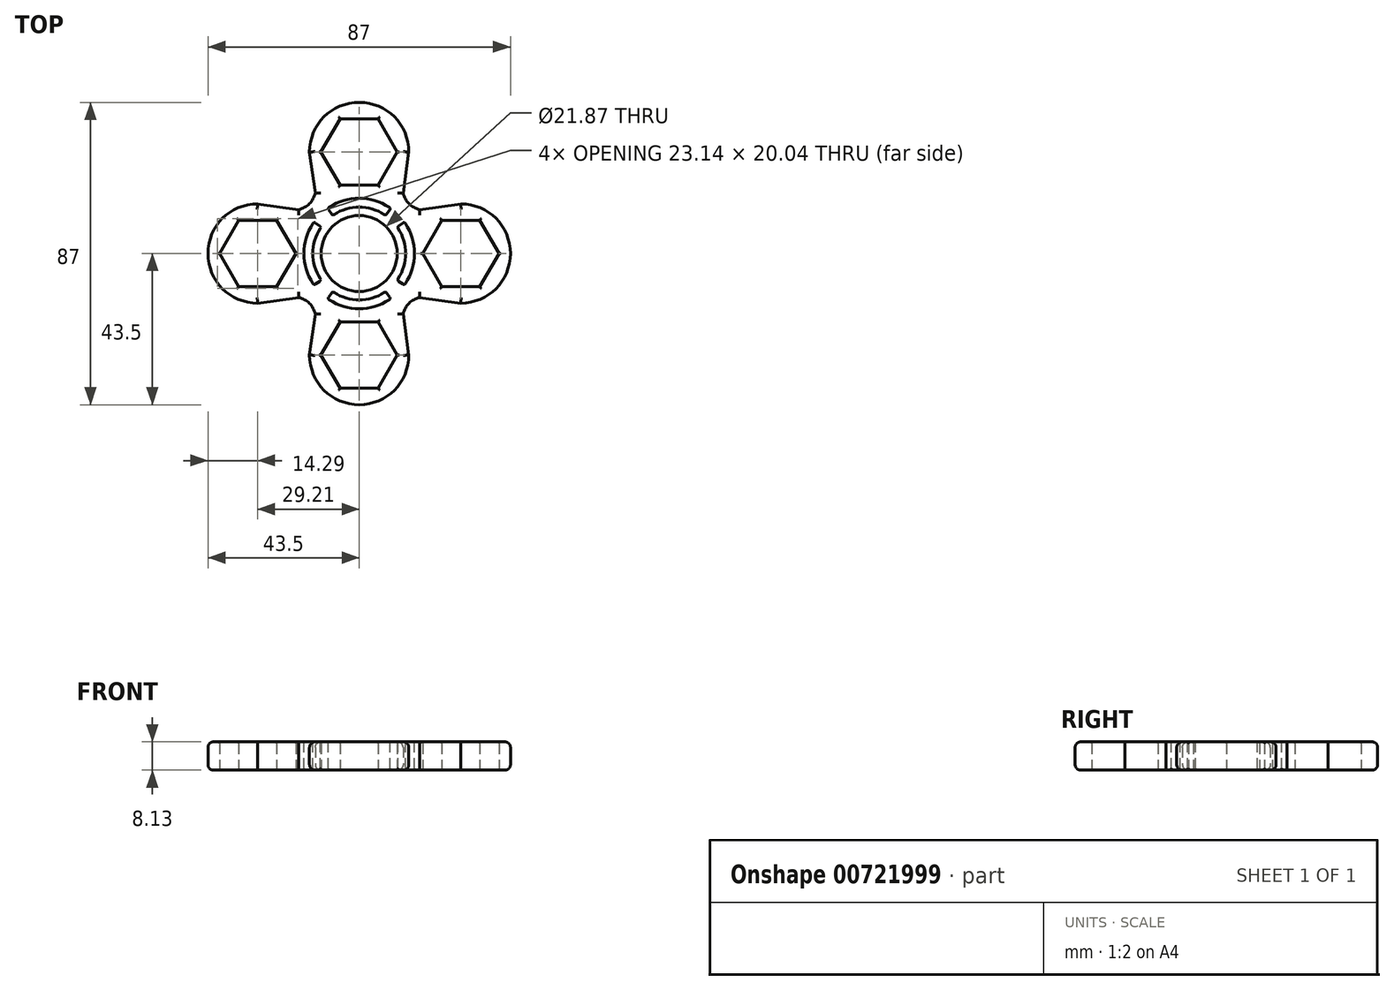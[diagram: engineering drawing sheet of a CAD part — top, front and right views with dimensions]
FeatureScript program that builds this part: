
annotation { "Feature Type Name" : "Feature", "Feature Type Description" : "" }
export const myFeature = defineFeature(function(context is Context, id is Id, definition is map)
    precondition{}
    {
        {
            var Q0;
            Q0=qCreatedBy(makeId("Top.planeOp"),FACE);
            var sketch = newSketch(context, id + "F0", { "sketchPlane" : qUnion([Q0])});
            skCircle(sketch, "E0", {"center": v(0, 0) * mm, "radius": 10.93 * mm});
            skLineSegment(sketch, "E1", {"start": v(0, 32.8) * mm, "end": v(0, -37.97) * mm, "construction": true});
            skLineSegment(sketch, "E2", {"start": v(-47.87, 0) * mm, "end": v(62.97, 0) * mm, "construction": true});
            skCircle(sketch, "E3", {"center": v(29.21, 0) * mm, "radius": 7.94 * mm});
            skCircle(sketch, "E4", {"center": v(0, 29.21) * mm, "radius": 7.94 * mm});
            skCircle(sketch, "E5", {"center": v(-29.21, 0) * mm, "radius": 7.94 * mm});
            skCircle(sketch, "E6", {"center": v(0, -29.21) * mm, "radius": 7.94 * mm});
            skArc(sketch, "E7", {"start": v(14.29, 29.21) * mm, "mid": v(0, 43.5) * mm, "end": v(-14.29, 29.21) * mm});
            skArc(sketch, "E8", {"start": v(29.21, -14.29) * mm, "mid": v(43.5, 0) * mm, "end": v(29.21, 14.29) * mm});
            skArc(sketch, "E9", {"start": v(-14.29, -29.21) * mm, "mid": v(0, -43.5) * mm, "end": v(14.29, -29.21) * mm});
            skArc(sketch, "E10", {"start": v(-29.21, 14.29) * mm, "mid": v(-43.5, 0) * mm, "end": v(-29.21, -14.29) * mm});
            skPoint(sketch, "E11.visualSharp", {"position": v(-11.05, 11.05) * mm});
            skArc(sketch, "E11.filletArc", {"start": v(-17.4, 12.64) * mm, "mid": v(-14.33, 14.33) * mm, "end": v(-12.64, 17.4) * mm});
            skPoint(sketch, "E12.visualSharp", {"position": v(11.05, 11.05) * mm});
            skArc(sketch, "E12.filletArc", {"start": v(12.64, 17.4) * mm, "mid": v(14.33, 14.33) * mm, "end": v(17.4, 12.64) * mm});
            skArc(sketch, "E13.MirrorCS", {"start": v(-17.4, -12.64) * mm, "mid": v(-14.33, -14.33) * mm, "end": v(-12.64, -17.4) * mm});
            skArc(sketch, "E14.MirrorCS", {"start": v(12.64, -17.4) * mm, "mid": v(14.33, -14.33) * mm, "end": v(17.4, -12.64) * mm});
            skLineSegment(sketch, "E15", {"start": v(-14.29, -29.21) * mm, "end": v(-12.64, -17.4) * mm});
            skLineSegment(sketch, "E16", {"start": v(14.29, -29.2) * mm, "end": v(12.64, -17.4) * mm});
            skLineSegment(sketch, "E17", {"start": v(17.4, -12.64) * mm, "end": v(29.21, -14.29) * mm});
            skLineSegment(sketch, "E18", {"start": v(17.4, 12.64) * mm, "end": v(29.21, 14.29) * mm});
            skLineSegment(sketch, "E19", {"start": v(12.64, 17.4) * mm, "end": v(14.29, 29.21) * mm});
            skLineSegment(sketch, "E20", {"start": v(-14.29, 29.21) * mm, "end": v(-12.64, 17.4) * mm});
            skLineSegment(sketch, "E21", {"start": v(-17.4, 12.64) * mm, "end": v(-29.2, 14.29) * mm});
            skLineSegment(sketch, "E22", {"start": v(-29.2, -14.29) * mm, "end": v(-17.4, -12.64) * mm});
            skCircle(sketch, "E23.cCircle", {"center": v(0, 29.21) * mm, "radius": 9.51 * mm, "construction": true});
            skLineSegment(sketch, "E23.0", {"start": v(10.99, 29.21) * mm, "end": v(5.5, 19.7) * mm});
            skLineSegment(sketch, "E23.1", {"start": v(5.5, 19.7) * mm, "end": v(-5.5, 19.7) * mm});
            skLineSegment(sketch, "E23.2", {"start": v(-5.5, 19.7) * mm, "end": v(-10.99, 29.21) * mm});
            skLineSegment(sketch, "E23.3", {"start": v(-10.99, 29.21) * mm, "end": v(-5.5, 38.72) * mm});
            skLineSegment(sketch, "E23.4", {"start": v(-5.5, 38.72) * mm, "end": v(5.5, 38.72) * mm});
            skLineSegment(sketch, "E23.5", {"start": v(5.5, 38.72) * mm, "end": v(10.99, 29.21) * mm});
            skPoint(sketch, "E23.0.midPoint", {"position": v(8.24, 24.45) * mm});
            skCircle(sketch, "E24.cCircle", {"center": v(29.21, 0) * mm, "radius": 9.51 * mm, "construction": true});
            skLineSegment(sketch, "E24.0", {"start": v(40.2, 0) * mm, "end": v(34.7, -9.51) * mm});
            skLineSegment(sketch, "E24.1", {"start": v(34.7, -9.51) * mm, "end": v(23.72, -9.51) * mm});
            skLineSegment(sketch, "E24.2", {"start": v(23.72, -9.51) * mm, "end": v(18.22, 0) * mm});
            skLineSegment(sketch, "E24.3", {"start": v(18.22, 0) * mm, "end": v(23.72, 9.51) * mm});
            skLineSegment(sketch, "E24.4", {"start": v(23.72, 9.51) * mm, "end": v(34.7, 9.51) * mm});
            skLineSegment(sketch, "E24.5", {"start": v(34.7, 9.51) * mm, "end": v(40.2, 0) * mm});
            skPoint(sketch, "E24.0.midPoint", {"position": v(37.45, -4.76) * mm});
            skCircle(sketch, "E25.cCircle", {"center": v(0, -29.21) * mm, "radius": 9.51 * mm, "construction": true});
            skLineSegment(sketch, "E25.0", {"start": v(10.99, -29.2) * mm, "end": v(5.5, -38.72) * mm});
            skLineSegment(sketch, "E25.1", {"start": v(5.5, -38.72) * mm, "end": v(-5.5, -38.72) * mm});
            skLineSegment(sketch, "E25.2", {"start": v(-5.5, -38.72) * mm, "end": v(-10.99, -29.2) * mm});
            skLineSegment(sketch, "E25.3", {"start": v(-10.99, -29.21) * mm, "end": v(-5.5, -19.7) * mm});
            skLineSegment(sketch, "E25.4", {"start": v(-5.5, -19.7) * mm, "end": v(5.5, -19.7) * mm});
            skLineSegment(sketch, "E25.5", {"start": v(5.5, -19.7) * mm, "end": v(10.99, -29.21) * mm});
            skPoint(sketch, "E25.0.midPoint", {"position": v(8.24, -33.97) * mm});
            skPoint(sketch, "E26.0.midPoint", {"position": v(-0.58, -16.53) * mm});
            skCircle(sketch, "E27.cCircle", {"center": v(-29.21, 0) * mm, "radius": 9.51 * mm, "construction": true});
            skLineSegment(sketch, "E27.0", {"start": v(-18.22, 0) * mm, "end": v(-23.72, -9.51) * mm});
            skLineSegment(sketch, "E27.1", {"start": v(-23.72, -9.51) * mm, "end": v(-34.7, -9.51) * mm});
            skLineSegment(sketch, "E27.2", {"start": v(-34.7, -9.51) * mm, "end": v(-40.2, 0) * mm});
            skLineSegment(sketch, "E27.3", {"start": v(-40.2, 0) * mm, "end": v(-34.7, 9.51) * mm});
            skLineSegment(sketch, "E27.4", {"start": v(-34.7, 9.51) * mm, "end": v(-23.72, 9.51) * mm});
            skLineSegment(sketch, "E27.5", {"start": v(-23.72, 9.51) * mm, "end": v(-18.22, 0) * mm});
            skPoint(sketch, "E27.0.midPoint", {"position": v(-20.97, -4.76) * mm});
            skSolve(sketch);
        }
        {
            var Q0;
            Q0=qSketchRegion(id+"F0",true);
            extrude(context, id + "F1", {"entities" : qUnion([Q0]), "depth" : 8.13 * mm, "offsetDistance" : 25.4 * mm});
        }
        {
            var Q0;
            Q0=makeQuery(id+"F1.opExtrude","CAP_EDGE",EDGE,{"disambiguationData":[OSD([sQuery(id+"F0.wireOp",EDGE,"E10")])],"isStart":true});
            var Q1;
            Q1=makeQuery(id+"F1.opExtrude","CAP_EDGE",EDGE,{"disambiguationData":[OSD([sQuery(id+"F0.wireOp",EDGE,"E22")])],"isStart":true});
            var Q2;
            Q2=makeQuery(id+"F1.opExtrude","CAP_EDGE",EDGE,{"disambiguationData":[OSD([sQuery(id+"F0.wireOp",EDGE,"E13.MirrorCS")])],"isStart":true});
            var Q3;
            Q3=makeQuery(id+"F1.opExtrude","CAP_EDGE",EDGE,{"disambiguationData":[OSD([sQuery(id+"F0.wireOp",EDGE,"E15")])],"isStart":true});
            var Q4;
            Q4=makeQuery(id+"F1.opExtrude","CAP_EDGE",EDGE,{"disambiguationData":[OSD([sQuery(id+"F0.wireOp",EDGE,"E9")])],"isStart":true});
            var Q5;
            Q5=makeQuery(id+"F1.opExtrude","CAP_EDGE",EDGE,{"disambiguationData":[OSD([sQuery(id+"F0.wireOp",EDGE,"E16")])],"isStart":true});
            var Q6;
            Q6=makeQuery(id+"F1.opExtrude","CAP_EDGE",EDGE,{"disambiguationData":[OSD([sQuery(id+"F0.wireOp",EDGE,"E14.MirrorCS")])],"isStart":true});
            var Q7;
            Q7=makeQuery(id+"F1.opExtrude","CAP_EDGE",EDGE,{"disambiguationData":[OSD([sQuery(id+"F0.wireOp",EDGE,"E17")])],"isStart":true});
            var Q8;
            Q8=makeQuery(id+"F1.opExtrude","CAP_EDGE",EDGE,{"disambiguationData":[OSD([sQuery(id+"F0.wireOp",EDGE,"E8")])],"isStart":true});
            var Q9;
            Q9=makeQuery(id+"F1.opExtrude","CAP_EDGE",EDGE,{"disambiguationData":[OSD([sQuery(id+"F0.wireOp",EDGE,"E18")])],"isStart":true});
            var Q10;
            Q10=makeQuery(id+"F1.opExtrude","CAP_EDGE",EDGE,{"disambiguationData":[OSD([sQuery(id+"F0.wireOp",EDGE,"E12.filletArc")])],"isStart":true});
            var Q11;
            Q11=makeQuery(id+"F1.opExtrude","CAP_EDGE",EDGE,{"disambiguationData":[OSD([sQuery(id+"F0.wireOp",EDGE,"E19")])],"isStart":true});
            var Q12;
            Q12=makeQuery(id+"F1.opExtrude","CAP_EDGE",EDGE,{"disambiguationData":[OSD([sQuery(id+"F0.wireOp",EDGE,"E7")])],"isStart":true});
            var Q13;
            Q13=makeQuery(id+"F1.opExtrude","CAP_EDGE",EDGE,{"disambiguationData":[OSD([sQuery(id+"F0.wireOp",EDGE,"E20")])],"isStart":true});
            var Q14;
            Q14=makeQuery(id+"F1.opExtrude","CAP_EDGE",EDGE,{"disambiguationData":[OSD([sQuery(id+"F0.wireOp",EDGE,"E11.filletArc")])],"isStart":true});
            var Q15;
            Q15=makeQuery(id+"F1.opExtrude","CAP_EDGE",EDGE,{"disambiguationData":[OSD([sQuery(id+"F0.wireOp",EDGE,"E21")])],"isStart":true});
            var Q16;
            Q16=makeQuery(id+"F1.opExtrude","CAP_EDGE",EDGE,{"disambiguationData":[OSD([sQuery(id+"F0.wireOp",EDGE,"E10")])],"isStart":false});
            var Q17;
            Q17=makeQuery(id+"F1.opExtrude","CAP_EDGE",EDGE,{"disambiguationData":[OSD([sQuery(id+"F0.wireOp",EDGE,"E22")])],"isStart":false});
            var Q18;
            Q18=makeQuery(id+"F1.opExtrude","CAP_EDGE",EDGE,{"disambiguationData":[OSD([sQuery(id+"F0.wireOp",EDGE,"E13.MirrorCS")])],"isStart":false});
            var Q19;
            Q19=makeQuery(id+"F1.opExtrude","CAP_EDGE",EDGE,{"disambiguationData":[OSD([sQuery(id+"F0.wireOp",EDGE,"E21")])],"isStart":false});
            var Q20;
            Q20=makeQuery(id+"F1.opExtrude","CAP_EDGE",EDGE,{"disambiguationData":[OSD([sQuery(id+"F0.wireOp",EDGE,"E11.filletArc")])],"isStart":false});
            var Q21;
            Q21=makeQuery(id+"F1.opExtrude","CAP_EDGE",EDGE,{"disambiguationData":[OSD([sQuery(id+"F0.wireOp",EDGE,"E20")])],"isStart":false});
            var Q22;
            Q22=makeQuery(id+"F1.opExtrude","CAP_EDGE",EDGE,{"disambiguationData":[OSD([sQuery(id+"F0.wireOp",EDGE,"E7")])],"isStart":false});
            var Q23;
            Q23=makeQuery(id+"F1.opExtrude","CAP_EDGE",EDGE,{"disambiguationData":[OSD([sQuery(id+"F0.wireOp",EDGE,"E19")])],"isStart":false});
            var Q24;
            Q24=makeQuery(id+"F1.opExtrude","CAP_EDGE",EDGE,{"disambiguationData":[OSD([sQuery(id+"F0.wireOp",EDGE,"E8")])],"isStart":false});
            var Q25;
            Q25=makeQuery(id+"F1.opExtrude","CAP_EDGE",EDGE,{"disambiguationData":[OSD([sQuery(id+"F0.wireOp",EDGE,"E17")])],"isStart":false});
            var Q26;
            Q26=makeQuery(id+"F1.opExtrude","CAP_EDGE",EDGE,{"disambiguationData":[OSD([sQuery(id+"F0.wireOp",EDGE,"E14.MirrorCS")])],"isStart":false});
            var Q27;
            Q27=makeQuery(id+"F1.opExtrude","CAP_EDGE",EDGE,{"disambiguationData":[OSD([sQuery(id+"F0.wireOp",EDGE,"E16")])],"isStart":false});
            var Q28;
            Q28=makeQuery(id+"F1.opExtrude","CAP_EDGE",EDGE,{"disambiguationData":[OSD([sQuery(id+"F0.wireOp",EDGE,"E9")])],"isStart":false});
            var Q29;
            Q29=makeQuery(id+"F1.opExtrude","CAP_EDGE",EDGE,{"disambiguationData":[OSD([sQuery(id+"F0.wireOp",EDGE,"E15")])],"isStart":false});
            var Q30;
            Q30=makeQuery(id+"F1.opExtrude","CAP_EDGE",EDGE,{"disambiguationData":[OSD([sQuery(id+"F0.wireOp",EDGE,"E12.filletArc")])],"isStart":false});
            var Q31;
            Q31=makeQuery(id+"F1.opExtrude","CAP_EDGE",EDGE,{"disambiguationData":[OSD([sQuery(id+"F0.wireOp",EDGE,"E18")])],"isStart":false});
            fillet(context, id + "F2", {"entities" : qUnion([Q0, Q1, Q2, Q3, Q4, Q5, Q6, Q7, Q8, Q9, Q10, Q11, Q12, Q13, Q14, Q15, Q16, Q17, Q18, Q19, Q20, Q21, Q22, Q23, Q24, Q25, Q26, Q27, Q28, Q29, Q30, Q31]), "radius" : 1.57 * mm, "allowEdgeOverflow" : false});
        }
        {
            var Q0;
            Q0=makeQuery(id+"F1.opExtrude","CAP_EDGE",EDGE,{"disambiguationData":[OSD([sQuery(id+"F0.wireOp",EDGE,"E5")])],"isStart":false});
            var Q1;
            Q1=makeQuery(id+"F1.opExtrude","CAP_EDGE",EDGE,{"disambiguationData":[OSD([sQuery(id+"F0.wireOp",EDGE,"E4")])],"isStart":false});
            var Q2;
            Q2=makeQuery(id+"F1.opExtrude","CAP_EDGE",EDGE,{"disambiguationData":[OSD([sQuery(id+"F0.wireOp",EDGE,"E0")])],"isStart":false});
            var Q3;
            Q3=makeQuery(id+"F1.opExtrude","CAP_EDGE",EDGE,{"disambiguationData":[OSD([sQuery(id+"F0.wireOp",EDGE,"E3")])],"isStart":false});
            var Q4;
            Q4=makeQuery(id+"F1.opExtrude","CAP_EDGE",EDGE,{"disambiguationData":[OSD([sQuery(id+"F0.wireOp",EDGE,"E6")])],"isStart":false});
            var Q5;
            Q5=makeQuery(id+"F1.opExtrude","CAP_EDGE",EDGE,{"disambiguationData":[OSD([sQuery(id+"F0.wireOp",EDGE,"E6")])],"isStart":true});
            var Q6;
            Q6=makeQuery(id+"F1.opExtrude","CAP_EDGE",EDGE,{"disambiguationData":[OSD([sQuery(id+"F0.wireOp",EDGE,"E5")])],"isStart":true});
            var Q7;
            Q7=makeQuery(id+"F1.opExtrude","CAP_EDGE",EDGE,{"disambiguationData":[OSD([sQuery(id+"F0.wireOp",EDGE,"E0")])],"isStart":true});
            var Q8;
            Q8=makeQuery(id+"F1.opExtrude","CAP_EDGE",EDGE,{"disambiguationData":[OSD([sQuery(id+"F0.wireOp",EDGE,"E3")])],"isStart":true});
            var Q9;
            Q9=makeQuery(id+"F1.opExtrude","CAP_EDGE",EDGE,{"disambiguationData":[OSD([sQuery(id+"F0.wireOp",EDGE,"E4")])],"isStart":true});
            fillet(context, id + "F3", {"entities" : qUnion([Q0, Q1, Q2, Q3, Q4, Q5, Q6, Q7, Q8, Q9]), "radius" : 0.5 * mm, "tangentPropagation" : true, "allowEdgeOverflow" : false});
        }
        {
            var Q0;
            Q0=makeQuery(id+"F1.opExtrude","CAP_EDGE",EDGE,{"disambiguationData":[OSD([sQuery(id+"F0.wireOp",EDGE,"E25.4")])],"isStart":false});
            var Q1;
            Q1=makeQuery(id+"F1.opExtrude","CAP_EDGE",EDGE,{"disambiguationData":[OSD([sQuery(id+"F0.wireOp",EDGE,"E24.4")])],"isStart":false});
            var Q2;
            Q2=makeQuery(id+"F1.opExtrude","CAP_EDGE",EDGE,{"disambiguationData":[OSD([sQuery(id+"F0.wireOp",EDGE,"E23.5")])],"isStart":false});
            var Q3;
            Q3=makeQuery(id+"F1.opExtrude","CAP_EDGE",EDGE,{"disambiguationData":[OSD([sQuery(id+"F0.wireOp",EDGE,"E27.5")])],"isStart":false});
            var Q4;
            Q4=makeQuery(id+"F1.opExtrude","CAP_EDGE",EDGE,{"disambiguationData":[OSD([sQuery(id+"F0.wireOp",EDGE,"E27.4")])],"isStart":false});
            var Q5;
            Q5=makeQuery(id+"F1.opExtrude","CAP_EDGE",EDGE,{"disambiguationData":[OSD([sQuery(id+"F0.wireOp",EDGE,"E27.3")])],"isStart":false});
            var Q6;
            Q6=makeQuery(id+"F1.opExtrude","CAP_EDGE",EDGE,{"disambiguationData":[OSD([sQuery(id+"F0.wireOp",EDGE,"E27.2")])],"isStart":false});
            var Q7;
            Q7=makeQuery(id+"F1.opExtrude","CAP_EDGE",EDGE,{"disambiguationData":[OSD([sQuery(id+"F0.wireOp",EDGE,"E27.1")])],"isStart":false});
            var Q8;
            Q8=makeQuery(id+"F1.opExtrude","CAP_EDGE",EDGE,{"disambiguationData":[OSD([sQuery(id+"F0.wireOp",EDGE,"E27.0")])],"isStart":false});
            var Q9;
            Q9=makeQuery(id+"F1.opExtrude","CAP_EDGE",EDGE,{"disambiguationData":[OSD([sQuery(id+"F0.wireOp",EDGE,"E25.3")])],"isStart":false});
            var Q10;
            Q10=makeQuery(id+"F1.opExtrude","CAP_EDGE",EDGE,{"disambiguationData":[OSD([sQuery(id+"F0.wireOp",EDGE,"E25.5")])],"isStart":false});
            var Q11;
            Q11=makeQuery(id+"F1.opExtrude","CAP_EDGE",EDGE,{"disambiguationData":[OSD([sQuery(id+"F0.wireOp",EDGE,"E25.0")])],"isStart":false});
            var Q12;
            Q12=makeQuery(id+"F1.opExtrude","CAP_EDGE",EDGE,{"disambiguationData":[OSD([sQuery(id+"F0.wireOp",EDGE,"E25.1")])],"isStart":false});
            var Q13;
            Q13=makeQuery(id+"F1.opExtrude","CAP_EDGE",EDGE,{"disambiguationData":[OSD([sQuery(id+"F0.wireOp",EDGE,"E25.2")])],"isStart":false});
            var Q14;
            Q14=makeQuery(id+"F1.opExtrude","CAP_EDGE",EDGE,{"disambiguationData":[OSD([sQuery(id+"F0.wireOp",EDGE,"E24.3")])],"isStart":false});
            var Q15;
            Q15=makeQuery(id+"F1.opExtrude","CAP_EDGE",EDGE,{"disambiguationData":[OSD([sQuery(id+"F0.wireOp",EDGE,"E24.2")])],"isStart":false});
            var Q16;
            Q16=makeQuery(id+"F1.opExtrude","CAP_EDGE",EDGE,{"disambiguationData":[OSD([sQuery(id+"F0.wireOp",EDGE,"E24.1")])],"isStart":false});
            var Q17;
            Q17=makeQuery(id+"F1.opExtrude","CAP_EDGE",EDGE,{"disambiguationData":[OSD([sQuery(id+"F0.wireOp",EDGE,"E24.0")])],"isStart":false});
            var Q18;
            Q18=makeQuery(id+"F1.opExtrude","CAP_EDGE",EDGE,{"disambiguationData":[OSD([sQuery(id+"F0.wireOp",EDGE,"E24.5")])],"isStart":false});
            var Q19;
            Q19=makeQuery(id+"F1.opExtrude","CAP_EDGE",EDGE,{"disambiguationData":[OSD([sQuery(id+"F0.wireOp",EDGE,"E23.0")])],"isStart":false});
            var Q20;
            Q20=makeQuery(id+"F1.opExtrude","CAP_EDGE",EDGE,{"disambiguationData":[OSD([sQuery(id+"F0.wireOp",EDGE,"E23.1")])],"isStart":false});
            var Q21;
            Q21=makeQuery(id+"F1.opExtrude","CAP_EDGE",EDGE,{"disambiguationData":[OSD([sQuery(id+"F0.wireOp",EDGE,"E23.2")])],"isStart":false});
            var Q22;
            Q22=makeQuery(id+"F1.opExtrude","CAP_EDGE",EDGE,{"disambiguationData":[OSD([sQuery(id+"F0.wireOp",EDGE,"E23.3")])],"isStart":false});
            var Q23;
            Q23=makeQuery(id+"F1.opExtrude","CAP_EDGE",EDGE,{"disambiguationData":[OSD([sQuery(id+"F0.wireOp",EDGE,"E23.4")])],"isStart":false});
            var Q24;
            Q24=makeQuery(id+"F1.opExtrude","CAP_EDGE",EDGE,{"disambiguationData":[OSD([sQuery(id+"F0.wireOp",EDGE,"E27.2")])],"isStart":true});
            var Q25;
            Q25=makeQuery(id+"F1.opExtrude","CAP_EDGE",EDGE,{"disambiguationData":[OSD([sQuery(id+"F0.wireOp",EDGE,"E27.1")])],"isStart":true});
            var Q26;
            Q26=makeQuery(id+"F1.opExtrude","CAP_EDGE",EDGE,{"disambiguationData":[OSD([sQuery(id+"F0.wireOp",EDGE,"E27.0")])],"isStart":true});
            var Q27;
            Q27=makeQuery(id+"F1.opExtrude","CAP_EDGE",EDGE,{"disambiguationData":[OSD([sQuery(id+"F0.wireOp",EDGE,"E27.5")])],"isStart":true});
            var Q28;
            Q28=makeQuery(id+"F1.opExtrude","CAP_EDGE",EDGE,{"disambiguationData":[OSD([sQuery(id+"F0.wireOp",EDGE,"E27.4")])],"isStart":true});
            var Q29;
            Q29=makeQuery(id+"F1.opExtrude","CAP_EDGE",EDGE,{"disambiguationData":[OSD([sQuery(id+"F0.wireOp",EDGE,"E27.3")])],"isStart":true});
            var Q30;
            Q30=makeQuery(id+"F1.opExtrude","CAP_EDGE",EDGE,{"disambiguationData":[OSD([sQuery(id+"F0.wireOp",EDGE,"E23.2")])],"isStart":true});
            var Q31;
            Q31=makeQuery(id+"F1.opExtrude","CAP_EDGE",EDGE,{"disambiguationData":[OSD([sQuery(id+"F0.wireOp",EDGE,"E23.1")])],"isStart":true});
            var Q32;
            Q32=makeQuery(id+"F1.opExtrude","CAP_EDGE",EDGE,{"disambiguationData":[OSD([sQuery(id+"F0.wireOp",EDGE,"E23.0")])],"isStart":true});
            var Q33;
            Q33=makeQuery(id+"F1.opExtrude","CAP_EDGE",EDGE,{"disambiguationData":[OSD([sQuery(id+"F0.wireOp",EDGE,"E23.5")])],"isStart":true});
            var Q34;
            Q34=makeQuery(id+"F1.opExtrude","CAP_EDGE",EDGE,{"disambiguationData":[OSD([sQuery(id+"F0.wireOp",EDGE,"E23.4")])],"isStart":true});
            var Q35;
            Q35=makeQuery(id+"F1.opExtrude","CAP_EDGE",EDGE,{"disambiguationData":[OSD([sQuery(id+"F0.wireOp",EDGE,"E23.3")])],"isStart":true});
            var Q36;
            Q36=makeQuery(id+"F1.opExtrude","CAP_EDGE",EDGE,{"disambiguationData":[OSD([sQuery(id+"F0.wireOp",EDGE,"E24.2")])],"isStart":true});
            var Q37;
            Q37=makeQuery(id+"F1.opExtrude","CAP_EDGE",EDGE,{"disambiguationData":[OSD([sQuery(id+"F0.wireOp",EDGE,"E24.1")])],"isStart":true});
            var Q38;
            Q38=makeQuery(id+"F1.opExtrude","CAP_EDGE",EDGE,{"disambiguationData":[OSD([sQuery(id+"F0.wireOp",EDGE,"E24.0")])],"isStart":true});
            var Q39;
            Q39=makeQuery(id+"F1.opExtrude","CAP_EDGE",EDGE,{"disambiguationData":[OSD([sQuery(id+"F0.wireOp",EDGE,"E24.5")])],"isStart":true});
            var Q40;
            Q40=makeQuery(id+"F1.opExtrude","CAP_EDGE",EDGE,{"disambiguationData":[OSD([sQuery(id+"F0.wireOp",EDGE,"E24.4")])],"isStart":true});
            var Q41;
            Q41=makeQuery(id+"F1.opExtrude","CAP_EDGE",EDGE,{"disambiguationData":[OSD([sQuery(id+"F0.wireOp",EDGE,"E24.3")])],"isStart":true});
            var Q42;
            Q42=makeQuery(id+"F1.opExtrude","CAP_EDGE",EDGE,{"disambiguationData":[OSD([sQuery(id+"F0.wireOp",EDGE,"E25.4")])],"isStart":true});
            var Q43;
            Q43=makeQuery(id+"F1.opExtrude","CAP_EDGE",EDGE,{"disambiguationData":[OSD([sQuery(id+"F0.wireOp",EDGE,"E25.3")])],"isStart":true});
            var Q44;
            Q44=makeQuery(id+"F1.opExtrude","CAP_EDGE",EDGE,{"disambiguationData":[OSD([sQuery(id+"F0.wireOp",EDGE,"E25.2")])],"isStart":true});
            var Q45;
            Q45=makeQuery(id+"F1.opExtrude","CAP_EDGE",EDGE,{"disambiguationData":[OSD([sQuery(id+"F0.wireOp",EDGE,"E25.1")])],"isStart":true});
            var Q46;
            Q46=makeQuery(id+"F1.opExtrude","CAP_EDGE",EDGE,{"disambiguationData":[OSD([sQuery(id+"F0.wireOp",EDGE,"E25.0")])],"isStart":true});
            var Q47;
            Q47=makeQuery(id+"F1.opExtrude","CAP_EDGE",EDGE,{"disambiguationData":[OSD([sQuery(id+"F0.wireOp",EDGE,"E25.5")])],"isStart":true});
            fillet(context, id + "F4", {"entities" : qUnion([Q0, Q1, Q2, Q3, Q4, Q5, Q6, Q7, Q8, Q9, Q10, Q11, Q12, Q13, Q14, Q15, Q16, Q17, Q18, Q19, Q20, Q21, Q22, Q23, Q24, Q25, Q26, Q27, Q28, Q29, Q30, Q31, Q32, Q33, Q34, Q35, Q36, Q37, Q38, Q39, Q40, Q41, Q42, Q43, Q44, Q45, Q46, Q47]), "radius" : 0.5 * mm, "tangentPropagation" : true, "allowEdgeOverflow" : false});
        }
        {
            var Q0;
            Q0=makeQuery(id+"F1.opExtrude","CAP_FACE",FACE,{"disambiguationData":[OSD([sQuery(id+"F0.wireOp",EDGE,"E0"),sQuery(id+"F0.wireOp",EDGE,"E7"),sQuery(id+"F0.wireOp",EDGE,"E8"),sQuery(id+"F0.wireOp",EDGE,"E9"),sQuery(id+"F0.wireOp",EDGE,"E10"),sQuery(id+"F0.wireOp",EDGE,"E11.filletArc"),sQuery(id+"F0.wireOp",EDGE,"E12.filletArc"),sQuery(id+"F0.wireOp",EDGE,"E13.MirrorCS"),sQuery(id+"F0.wireOp",EDGE,"E14.MirrorCS"),sQuery(id+"F0.wireOp",EDGE,"E15"),sQuery(id+"F0.wireOp",EDGE,"E16"),sQuery(id+"F0.wireOp",EDGE,"E17"),sQuery(id+"F0.wireOp",EDGE,"E18"),sQuery(id+"F0.wireOp",EDGE,"E19"),sQuery(id+"F0.wireOp",EDGE,"E20"),sQuery(id+"F0.wireOp",EDGE,"E21"),sQuery(id+"F0.wireOp",EDGE,"E22"),sQuery(id+"F0.wireOp",EDGE,"E23.0"),sQuery(id+"F0.wireOp",EDGE,"E23.1"),sQuery(id+"F0.wireOp",EDGE,"E23.2"),sQuery(id+"F0.wireOp",EDGE,"E23.3"),sQuery(id+"F0.wireOp",EDGE,"E23.4"),sQuery(id+"F0.wireOp",EDGE,"E23.5"),sQuery(id+"F0.wireOp",EDGE,"E24.0"),sQuery(id+"F0.wireOp",EDGE,"E24.1"),sQuery(id+"F0.wireOp",EDGE,"E24.2"),sQuery(id+"F0.wireOp",EDGE,"E24.3"),sQuery(id+"F0.wireOp",EDGE,"E24.4"),sQuery(id+"F0.wireOp",EDGE,"E24.5"),sQuery(id+"F0.wireOp",EDGE,"E25.0"),sQuery(id+"F0.wireOp",EDGE,"E25.1"),sQuery(id+"F0.wireOp",EDGE,"E25.2"),sQuery(id+"F0.wireOp",EDGE,"E25.3"),sQuery(id+"F0.wireOp",EDGE,"E25.4"),sQuery(id+"F0.wireOp",EDGE,"E25.5"),sQuery(id+"F0.wireOp",EDGE,"E27.0"),sQuery(id+"F0.wireOp",EDGE,"E27.1"),sQuery(id+"F0.wireOp",EDGE,"E27.2"),sQuery(id+"F0.wireOp",EDGE,"E27.3"),sQuery(id+"F0.wireOp",EDGE,"E27.4"),sQuery(id+"F0.wireOp",EDGE,"E27.5")])],"isStart":false});
            var sketch = newSketch(context, id + "F5", { "sketchPlane" : qUnion([Q0])});
            skLineSegment(sketch, "E28", {"start": v(0, 19.96) * mm, "end": v(0, -20.08) * mm, "construction": true});
            skLineSegment(sketch, "E29", {"start": v(-9.1, 13) * mm, "end": v(-7.65, 10.92) * mm});
            skLineSegment(sketch, "E30", {"start": v(9.1, 13) * mm, "end": v(7.65, 10.92) * mm});
            skArc(sketch, "E31", {"start": v(9.1, 13) * mm, "mid": v(0, 15.88) * mm, "end": v(-9.1, 13) * mm});
            skArc(sketch, "E32", {"start": v(7.65, 10.92) * mm, "mid": v(0, 13.34) * mm, "end": v(-7.65, 10.92) * mm});
            skArc(sketch, "E33.1.0", {"start": v(-13, 9.1) * mm, "mid": v(-15.88, 0) * mm, "end": v(-13, -9.1) * mm});
            skLineSegment(sketch, "E33.1.1", {"start": v(-13, -9.1) * mm, "end": v(-10.92, -7.65) * mm});
            skArc(sketch, "E33.1.2", {"start": v(-10.92, 7.65) * mm, "mid": v(-13.34, 0) * mm, "end": v(-10.92, -7.65) * mm});
            skLineSegment(sketch, "E33.1.3", {"start": v(-13, 9.1) * mm, "end": v(-10.92, 7.65) * mm});
            skArc(sketch, "E33.2.0", {"start": v(-9.1, -13) * mm, "mid": v(0, -15.87) * mm, "end": v(9.1, -13) * mm});
            skLineSegment(sketch, "E33.2.1", {"start": v(9.1, -13) * mm, "end": v(7.65, -10.92) * mm});
            skArc(sketch, "E33.2.2", {"start": v(-7.65, -10.92) * mm, "mid": v(0, -13.33) * mm, "end": v(7.65, -10.92) * mm});
            skLineSegment(sketch, "E33.2.3", {"start": v(-9.1, -13) * mm, "end": v(-7.65, -10.92) * mm});
            skLineSegment(sketch, "E34.4.3.0", {"start": v(13, 9.1) * mm, "end": v(10.92, 7.65) * mm});
            skArc(sketch, "E34.6.3.0", {"start": v(13, -9.1) * mm, "mid": v(15.87, 0) * mm, "end": v(13, 9.1) * mm});
            skArc(sketch, "E34.7.3.0", {"start": v(10.92, -7.65) * mm, "mid": v(13.34, 0) * mm, "end": v(10.92, 7.65) * mm});
            skLineSegment(sketch, "E34.11.3.0", {"start": v(13, -9.1) * mm, "end": v(10.92, -7.65) * mm});
            skSolve(sketch);
        }
        {
            var Q0;
            Q0=qSketchRegion(id+"F5",true);
            extrude(context, id + "F6", {"entities" : qUnion([Q0]), "operationType" : NewBodyOperationType.REMOVE, "oppositeDirection" : true, "depth" : 25.4 * mm, "offsetDistance" : 25.4 * mm});
        }
        {
            var Q0;
            Q0=makeQuery(id+"F6.boolean.opBoolean","COPY",EDGE,{"derivedFrom":makeQuery(id+"F6.opExtrude","SWEPT_EDGE",EDGE,{"disambiguationData":[OSD([sQuery(id+"F5.wireOp",EDGE,"E30"),sQuery(id+"F5.wireOp",EDGE,"E31")])]})});
            var Q1;
            Q1=makeQuery(id+"F6.boolean.opBoolean","COPY",EDGE,{"derivedFrom":makeQuery(id+"F6.opExtrude","SWEPT_EDGE",EDGE,{"disambiguationData":[OSD([sQuery(id+"F5.wireOp",EDGE,"E30"),sQuery(id+"F5.wireOp",EDGE,"E32")])]})});
            var Q2;
            Q2=makeQuery(id+"F6.boolean.opBoolean","COPY",EDGE,{"derivedFrom":makeQuery(id+"F6.opExtrude","CAP_EDGE",EDGE,{"disambiguationData":[OSD([sQuery(id+"F5.wireOp",EDGE,"E30")])],"isStart":true})});
            var Q3;
            Q3=makeQuery(id+"F6.boolean.opBoolean","COPY",EDGE,{"derivedFrom":makeQuery(id+"F6.opExtrude","SWEPT_EDGE",EDGE,{"disambiguationData":[OSD([sQuery(id+"F5.wireOp",EDGE,"E29"),sQuery(id+"F5.wireOp",EDGE,"E31")])]})});
            var Q4;
            Q4=makeQuery(id+"F6.boolean.opBoolean","COPY",EDGE,{"derivedFrom":makeQuery(id+"F6.opExtrude","SWEPT_EDGE",EDGE,{"disambiguationData":[OSD([sQuery(id+"F5.wireOp",EDGE,"E29"),sQuery(id+"F5.wireOp",EDGE,"E32")])]})});
            var Q5;
            Q5=makeQuery(id+"F6.boolean.opBoolean","INTERSECT",EDGE,{"derivedFrom":[makeQuery(id+"F1.opExtrude","CAP_FACE",FACE,{"disambiguationData":[OSD([sQuery(id+"F0.wireOp",EDGE,"E0"),sQuery(id+"F0.wireOp",EDGE,"E7"),sQuery(id+"F0.wireOp",EDGE,"E8"),sQuery(id+"F0.wireOp",EDGE,"E9"),sQuery(id+"F0.wireOp",EDGE,"E10"),sQuery(id+"F0.wireOp",EDGE,"E11.filletArc"),sQuery(id+"F0.wireOp",EDGE,"E12.filletArc"),sQuery(id+"F0.wireOp",EDGE,"E13.MirrorCS"),sQuery(id+"F0.wireOp",EDGE,"E14.MirrorCS"),sQuery(id+"F0.wireOp",EDGE,"E15"),sQuery(id+"F0.wireOp",EDGE,"E16"),sQuery(id+"F0.wireOp",EDGE,"E17"),sQuery(id+"F0.wireOp",EDGE,"E18"),sQuery(id+"F0.wireOp",EDGE,"E19"),sQuery(id+"F0.wireOp",EDGE,"E20"),sQuery(id+"F0.wireOp",EDGE,"E21"),sQuery(id+"F0.wireOp",EDGE,"E22"),sQuery(id+"F0.wireOp",EDGE,"E23.0"),sQuery(id+"F0.wireOp",EDGE,"E23.1"),sQuery(id+"F0.wireOp",EDGE,"E23.2"),sQuery(id+"F0.wireOp",EDGE,"E23.3"),sQuery(id+"F0.wireOp",EDGE,"E23.4"),sQuery(id+"F0.wireOp",EDGE,"E23.5"),sQuery(id+"F0.wireOp",EDGE,"E24.0"),sQuery(id+"F0.wireOp",EDGE,"E24.1"),sQuery(id+"F0.wireOp",EDGE,"E24.2"),sQuery(id+"F0.wireOp",EDGE,"E24.3"),sQuery(id+"F0.wireOp",EDGE,"E24.4"),sQuery(id+"F0.wireOp",EDGE,"E24.5"),sQuery(id+"F0.wireOp",EDGE,"E25.0"),sQuery(id+"F0.wireOp",EDGE,"E25.1"),sQuery(id+"F0.wireOp",EDGE,"E25.2"),sQuery(id+"F0.wireOp",EDGE,"E25.3"),sQuery(id+"F0.wireOp",EDGE,"E25.4"),sQuery(id+"F0.wireOp",EDGE,"E25.5"),sQuery(id+"F0.wireOp",EDGE,"E27.0"),sQuery(id+"F0.wireOp",EDGE,"E27.1"),sQuery(id+"F0.wireOp",EDGE,"E27.2"),sQuery(id+"F0.wireOp",EDGE,"E27.3"),sQuery(id+"F0.wireOp",EDGE,"E27.4"),sQuery(id+"F0.wireOp",EDGE,"E27.5")])],"isStart":true}),makeQuery(id+"F6.opExtrude","SWEPT_FACE",FACE,{"disambiguationData":[OSD([sQuery(id+"F5.wireOp",EDGE,"E31")])]})]});
            var Q6;
            Q6=makeQuery(id+"F6.boolean.opBoolean","COPY",EDGE,{"derivedFrom":makeQuery(id+"F6.opExtrude","CAP_EDGE",EDGE,{"disambiguationData":[OSD([sQuery(id+"F5.wireOp",EDGE,"E33.1.3")])],"isStart":true})});
            var Q7;
            Q7=makeQuery(id+"F6.boolean.opBoolean","COPY",EDGE,{"derivedFrom":makeQuery(id+"F6.opExtrude","CAP_EDGE",EDGE,{"disambiguationData":[OSD([sQuery(id+"F5.wireOp",EDGE,"E34.6.3.0")])],"isStart":true})});
            var Q8;
            Q8=makeQuery(id+"F6.boolean.opBoolean","COPY",EDGE,{"derivedFrom":makeQuery(id+"F6.opExtrude","CAP_EDGE",EDGE,{"disambiguationData":[OSD([sQuery(id+"F5.wireOp",EDGE,"E33.2.0")])],"isStart":true})});
            var Q9;
            Q9=makeQuery(id+"F6.boolean.opBoolean","INTERSECT",EDGE,{"derivedFrom":[makeQuery(id+"F1.opExtrude","CAP_FACE",FACE,{"disambiguationData":[OSD([sQuery(id+"F0.wireOp",EDGE,"E0"),sQuery(id+"F0.wireOp",EDGE,"E7"),sQuery(id+"F0.wireOp",EDGE,"E8"),sQuery(id+"F0.wireOp",EDGE,"E9"),sQuery(id+"F0.wireOp",EDGE,"E10"),sQuery(id+"F0.wireOp",EDGE,"E11.filletArc"),sQuery(id+"F0.wireOp",EDGE,"E12.filletArc"),sQuery(id+"F0.wireOp",EDGE,"E13.MirrorCS"),sQuery(id+"F0.wireOp",EDGE,"E14.MirrorCS"),sQuery(id+"F0.wireOp",EDGE,"E15"),sQuery(id+"F0.wireOp",EDGE,"E16"),sQuery(id+"F0.wireOp",EDGE,"E17"),sQuery(id+"F0.wireOp",EDGE,"E18"),sQuery(id+"F0.wireOp",EDGE,"E19"),sQuery(id+"F0.wireOp",EDGE,"E20"),sQuery(id+"F0.wireOp",EDGE,"E21"),sQuery(id+"F0.wireOp",EDGE,"E22"),sQuery(id+"F0.wireOp",EDGE,"E23.0"),sQuery(id+"F0.wireOp",EDGE,"E23.1"),sQuery(id+"F0.wireOp",EDGE,"E23.2"),sQuery(id+"F0.wireOp",EDGE,"E23.3"),sQuery(id+"F0.wireOp",EDGE,"E23.4"),sQuery(id+"F0.wireOp",EDGE,"E23.5"),sQuery(id+"F0.wireOp",EDGE,"E24.0"),sQuery(id+"F0.wireOp",EDGE,"E24.1"),sQuery(id+"F0.wireOp",EDGE,"E24.2"),sQuery(id+"F0.wireOp",EDGE,"E24.3"),sQuery(id+"F0.wireOp",EDGE,"E24.4"),sQuery(id+"F0.wireOp",EDGE,"E24.5"),sQuery(id+"F0.wireOp",EDGE,"E25.0"),sQuery(id+"F0.wireOp",EDGE,"E25.1"),sQuery(id+"F0.wireOp",EDGE,"E25.2"),sQuery(id+"F0.wireOp",EDGE,"E25.3"),sQuery(id+"F0.wireOp",EDGE,"E25.4"),sQuery(id+"F0.wireOp",EDGE,"E25.5"),sQuery(id+"F0.wireOp",EDGE,"E27.0"),sQuery(id+"F0.wireOp",EDGE,"E27.1"),sQuery(id+"F0.wireOp",EDGE,"E27.2"),sQuery(id+"F0.wireOp",EDGE,"E27.3"),sQuery(id+"F0.wireOp",EDGE,"E27.4"),sQuery(id+"F0.wireOp",EDGE,"E27.5")])],"isStart":true}),makeQuery(id+"F6.opExtrude","SWEPT_FACE",FACE,{"disambiguationData":[OSD([sQuery(id+"F5.wireOp",EDGE,"E33.2.0")])]})]});
            var Q10;
            Q10=makeQuery(id+"F6.boolean.opBoolean","INTERSECT",EDGE,{"derivedFrom":[makeQuery(id+"F1.opExtrude","CAP_FACE",FACE,{"disambiguationData":[OSD([sQuery(id+"F0.wireOp",EDGE,"E0"),sQuery(id+"F0.wireOp",EDGE,"E7"),sQuery(id+"F0.wireOp",EDGE,"E8"),sQuery(id+"F0.wireOp",EDGE,"E9"),sQuery(id+"F0.wireOp",EDGE,"E10"),sQuery(id+"F0.wireOp",EDGE,"E11.filletArc"),sQuery(id+"F0.wireOp",EDGE,"E12.filletArc"),sQuery(id+"F0.wireOp",EDGE,"E13.MirrorCS"),sQuery(id+"F0.wireOp",EDGE,"E14.MirrorCS"),sQuery(id+"F0.wireOp",EDGE,"E15"),sQuery(id+"F0.wireOp",EDGE,"E16"),sQuery(id+"F0.wireOp",EDGE,"E17"),sQuery(id+"F0.wireOp",EDGE,"E18"),sQuery(id+"F0.wireOp",EDGE,"E19"),sQuery(id+"F0.wireOp",EDGE,"E20"),sQuery(id+"F0.wireOp",EDGE,"E21"),sQuery(id+"F0.wireOp",EDGE,"E22"),sQuery(id+"F0.wireOp",EDGE,"E23.0"),sQuery(id+"F0.wireOp",EDGE,"E23.1"),sQuery(id+"F0.wireOp",EDGE,"E23.2"),sQuery(id+"F0.wireOp",EDGE,"E23.3"),sQuery(id+"F0.wireOp",EDGE,"E23.4"),sQuery(id+"F0.wireOp",EDGE,"E23.5"),sQuery(id+"F0.wireOp",EDGE,"E24.0"),sQuery(id+"F0.wireOp",EDGE,"E24.1"),sQuery(id+"F0.wireOp",EDGE,"E24.2"),sQuery(id+"F0.wireOp",EDGE,"E24.3"),sQuery(id+"F0.wireOp",EDGE,"E24.4"),sQuery(id+"F0.wireOp",EDGE,"E24.5"),sQuery(id+"F0.wireOp",EDGE,"E25.0"),sQuery(id+"F0.wireOp",EDGE,"E25.1"),sQuery(id+"F0.wireOp",EDGE,"E25.2"),sQuery(id+"F0.wireOp",EDGE,"E25.3"),sQuery(id+"F0.wireOp",EDGE,"E25.4"),sQuery(id+"F0.wireOp",EDGE,"E25.5"),sQuery(id+"F0.wireOp",EDGE,"E27.0"),sQuery(id+"F0.wireOp",EDGE,"E27.1"),sQuery(id+"F0.wireOp",EDGE,"E27.2"),sQuery(id+"F0.wireOp",EDGE,"E27.3"),sQuery(id+"F0.wireOp",EDGE,"E27.4"),sQuery(id+"F0.wireOp",EDGE,"E27.5")])],"isStart":true}),makeQuery(id+"F6.opExtrude","SWEPT_FACE",FACE,{"disambiguationData":[OSD([sQuery(id+"F5.wireOp",EDGE,"E33.2.2")])]})]});
            var Q11;
            Q11=makeQuery(id+"F6.boolean.opBoolean","INTERSECT",EDGE,{"derivedFrom":[makeQuery(id+"F1.opExtrude","CAP_FACE",FACE,{"disambiguationData":[OSD([sQuery(id+"F0.wireOp",EDGE,"E0"),sQuery(id+"F0.wireOp",EDGE,"E7"),sQuery(id+"F0.wireOp",EDGE,"E8"),sQuery(id+"F0.wireOp",EDGE,"E9"),sQuery(id+"F0.wireOp",EDGE,"E10"),sQuery(id+"F0.wireOp",EDGE,"E11.filletArc"),sQuery(id+"F0.wireOp",EDGE,"E12.filletArc"),sQuery(id+"F0.wireOp",EDGE,"E13.MirrorCS"),sQuery(id+"F0.wireOp",EDGE,"E14.MirrorCS"),sQuery(id+"F0.wireOp",EDGE,"E15"),sQuery(id+"F0.wireOp",EDGE,"E16"),sQuery(id+"F0.wireOp",EDGE,"E17"),sQuery(id+"F0.wireOp",EDGE,"E18"),sQuery(id+"F0.wireOp",EDGE,"E19"),sQuery(id+"F0.wireOp",EDGE,"E20"),sQuery(id+"F0.wireOp",EDGE,"E21"),sQuery(id+"F0.wireOp",EDGE,"E22"),sQuery(id+"F0.wireOp",EDGE,"E23.0"),sQuery(id+"F0.wireOp",EDGE,"E23.1"),sQuery(id+"F0.wireOp",EDGE,"E23.2"),sQuery(id+"F0.wireOp",EDGE,"E23.3"),sQuery(id+"F0.wireOp",EDGE,"E23.4"),sQuery(id+"F0.wireOp",EDGE,"E23.5"),sQuery(id+"F0.wireOp",EDGE,"E24.0"),sQuery(id+"F0.wireOp",EDGE,"E24.1"),sQuery(id+"F0.wireOp",EDGE,"E24.2"),sQuery(id+"F0.wireOp",EDGE,"E24.3"),sQuery(id+"F0.wireOp",EDGE,"E24.4"),sQuery(id+"F0.wireOp",EDGE,"E24.5"),sQuery(id+"F0.wireOp",EDGE,"E25.0"),sQuery(id+"F0.wireOp",EDGE,"E25.1"),sQuery(id+"F0.wireOp",EDGE,"E25.2"),sQuery(id+"F0.wireOp",EDGE,"E25.3"),sQuery(id+"F0.wireOp",EDGE,"E25.4"),sQuery(id+"F0.wireOp",EDGE,"E25.5"),sQuery(id+"F0.wireOp",EDGE,"E27.0"),sQuery(id+"F0.wireOp",EDGE,"E27.1"),sQuery(id+"F0.wireOp",EDGE,"E27.2"),sQuery(id+"F0.wireOp",EDGE,"E27.3"),sQuery(id+"F0.wireOp",EDGE,"E27.4"),sQuery(id+"F0.wireOp",EDGE,"E27.5")])],"isStart":true}),makeQuery(id+"F6.opExtrude","SWEPT_FACE",FACE,{"disambiguationData":[OSD([sQuery(id+"F5.wireOp",EDGE,"E33.1.0")])]})]});
            var Q12;
            Q12=makeQuery(id+"F6.boolean.opBoolean","INTERSECT",EDGE,{"derivedFrom":[makeQuery(id+"F1.opExtrude","CAP_FACE",FACE,{"disambiguationData":[OSD([sQuery(id+"F0.wireOp",EDGE,"E0"),sQuery(id+"F0.wireOp",EDGE,"E7"),sQuery(id+"F0.wireOp",EDGE,"E8"),sQuery(id+"F0.wireOp",EDGE,"E9"),sQuery(id+"F0.wireOp",EDGE,"E10"),sQuery(id+"F0.wireOp",EDGE,"E11.filletArc"),sQuery(id+"F0.wireOp",EDGE,"E12.filletArc"),sQuery(id+"F0.wireOp",EDGE,"E13.MirrorCS"),sQuery(id+"F0.wireOp",EDGE,"E14.MirrorCS"),sQuery(id+"F0.wireOp",EDGE,"E15"),sQuery(id+"F0.wireOp",EDGE,"E16"),sQuery(id+"F0.wireOp",EDGE,"E17"),sQuery(id+"F0.wireOp",EDGE,"E18"),sQuery(id+"F0.wireOp",EDGE,"E19"),sQuery(id+"F0.wireOp",EDGE,"E20"),sQuery(id+"F0.wireOp",EDGE,"E21"),sQuery(id+"F0.wireOp",EDGE,"E22"),sQuery(id+"F0.wireOp",EDGE,"E23.0"),sQuery(id+"F0.wireOp",EDGE,"E23.1"),sQuery(id+"F0.wireOp",EDGE,"E23.2"),sQuery(id+"F0.wireOp",EDGE,"E23.3"),sQuery(id+"F0.wireOp",EDGE,"E23.4"),sQuery(id+"F0.wireOp",EDGE,"E23.5"),sQuery(id+"F0.wireOp",EDGE,"E24.0"),sQuery(id+"F0.wireOp",EDGE,"E24.1"),sQuery(id+"F0.wireOp",EDGE,"E24.2"),sQuery(id+"F0.wireOp",EDGE,"E24.3"),sQuery(id+"F0.wireOp",EDGE,"E24.4"),sQuery(id+"F0.wireOp",EDGE,"E24.5"),sQuery(id+"F0.wireOp",EDGE,"E25.0"),sQuery(id+"F0.wireOp",EDGE,"E25.1"),sQuery(id+"F0.wireOp",EDGE,"E25.2"),sQuery(id+"F0.wireOp",EDGE,"E25.3"),sQuery(id+"F0.wireOp",EDGE,"E25.4"),sQuery(id+"F0.wireOp",EDGE,"E25.5"),sQuery(id+"F0.wireOp",EDGE,"E27.0"),sQuery(id+"F0.wireOp",EDGE,"E27.1"),sQuery(id+"F0.wireOp",EDGE,"E27.2"),sQuery(id+"F0.wireOp",EDGE,"E27.3"),sQuery(id+"F0.wireOp",EDGE,"E27.4"),sQuery(id+"F0.wireOp",EDGE,"E27.5")])],"isStart":true}),makeQuery(id+"F6.opExtrude","SWEPT_FACE",FACE,{"disambiguationData":[OSD([sQuery(id+"F5.wireOp",EDGE,"E33.1.2")])]})]});
            var Q13;
            Q13=makeQuery(id+"F6.boolean.opBoolean","INTERSECT",EDGE,{"derivedFrom":[makeQuery(id+"F1.opExtrude","CAP_FACE",FACE,{"disambiguationData":[OSD([sQuery(id+"F0.wireOp",EDGE,"E0"),sQuery(id+"F0.wireOp",EDGE,"E7"),sQuery(id+"F0.wireOp",EDGE,"E8"),sQuery(id+"F0.wireOp",EDGE,"E9"),sQuery(id+"F0.wireOp",EDGE,"E10"),sQuery(id+"F0.wireOp",EDGE,"E11.filletArc"),sQuery(id+"F0.wireOp",EDGE,"E12.filletArc"),sQuery(id+"F0.wireOp",EDGE,"E13.MirrorCS"),sQuery(id+"F0.wireOp",EDGE,"E14.MirrorCS"),sQuery(id+"F0.wireOp",EDGE,"E15"),sQuery(id+"F0.wireOp",EDGE,"E16"),sQuery(id+"F0.wireOp",EDGE,"E17"),sQuery(id+"F0.wireOp",EDGE,"E18"),sQuery(id+"F0.wireOp",EDGE,"E19"),sQuery(id+"F0.wireOp",EDGE,"E20"),sQuery(id+"F0.wireOp",EDGE,"E21"),sQuery(id+"F0.wireOp",EDGE,"E22"),sQuery(id+"F0.wireOp",EDGE,"E23.0"),sQuery(id+"F0.wireOp",EDGE,"E23.1"),sQuery(id+"F0.wireOp",EDGE,"E23.2"),sQuery(id+"F0.wireOp",EDGE,"E23.3"),sQuery(id+"F0.wireOp",EDGE,"E23.4"),sQuery(id+"F0.wireOp",EDGE,"E23.5"),sQuery(id+"F0.wireOp",EDGE,"E24.0"),sQuery(id+"F0.wireOp",EDGE,"E24.1"),sQuery(id+"F0.wireOp",EDGE,"E24.2"),sQuery(id+"F0.wireOp",EDGE,"E24.3"),sQuery(id+"F0.wireOp",EDGE,"E24.4"),sQuery(id+"F0.wireOp",EDGE,"E24.5"),sQuery(id+"F0.wireOp",EDGE,"E25.0"),sQuery(id+"F0.wireOp",EDGE,"E25.1"),sQuery(id+"F0.wireOp",EDGE,"E25.2"),sQuery(id+"F0.wireOp",EDGE,"E25.3"),sQuery(id+"F0.wireOp",EDGE,"E25.4"),sQuery(id+"F0.wireOp",EDGE,"E25.5"),sQuery(id+"F0.wireOp",EDGE,"E27.0"),sQuery(id+"F0.wireOp",EDGE,"E27.1"),sQuery(id+"F0.wireOp",EDGE,"E27.2"),sQuery(id+"F0.wireOp",EDGE,"E27.3"),sQuery(id+"F0.wireOp",EDGE,"E27.4"),sQuery(id+"F0.wireOp",EDGE,"E27.5")])],"isStart":true}),makeQuery(id+"F6.opExtrude","SWEPT_FACE",FACE,{"disambiguationData":[OSD([sQuery(id+"F5.wireOp",EDGE,"E33.1.1")])]})]});
            var Q14;
            Q14=makeQuery(id+"F6.boolean.opBoolean","INTERSECT",EDGE,{"derivedFrom":[makeQuery(id+"F1.opExtrude","CAP_FACE",FACE,{"disambiguationData":[OSD([sQuery(id+"F0.wireOp",EDGE,"E0"),sQuery(id+"F0.wireOp",EDGE,"E7"),sQuery(id+"F0.wireOp",EDGE,"E8"),sQuery(id+"F0.wireOp",EDGE,"E9"),sQuery(id+"F0.wireOp",EDGE,"E10"),sQuery(id+"F0.wireOp",EDGE,"E11.filletArc"),sQuery(id+"F0.wireOp",EDGE,"E12.filletArc"),sQuery(id+"F0.wireOp",EDGE,"E13.MirrorCS"),sQuery(id+"F0.wireOp",EDGE,"E14.MirrorCS"),sQuery(id+"F0.wireOp",EDGE,"E15"),sQuery(id+"F0.wireOp",EDGE,"E16"),sQuery(id+"F0.wireOp",EDGE,"E17"),sQuery(id+"F0.wireOp",EDGE,"E18"),sQuery(id+"F0.wireOp",EDGE,"E19"),sQuery(id+"F0.wireOp",EDGE,"E20"),sQuery(id+"F0.wireOp",EDGE,"E21"),sQuery(id+"F0.wireOp",EDGE,"E22"),sQuery(id+"F0.wireOp",EDGE,"E23.0"),sQuery(id+"F0.wireOp",EDGE,"E23.1"),sQuery(id+"F0.wireOp",EDGE,"E23.2"),sQuery(id+"F0.wireOp",EDGE,"E23.3"),sQuery(id+"F0.wireOp",EDGE,"E23.4"),sQuery(id+"F0.wireOp",EDGE,"E23.5"),sQuery(id+"F0.wireOp",EDGE,"E24.0"),sQuery(id+"F0.wireOp",EDGE,"E24.1"),sQuery(id+"F0.wireOp",EDGE,"E24.2"),sQuery(id+"F0.wireOp",EDGE,"E24.3"),sQuery(id+"F0.wireOp",EDGE,"E24.4"),sQuery(id+"F0.wireOp",EDGE,"E24.5"),sQuery(id+"F0.wireOp",EDGE,"E25.0"),sQuery(id+"F0.wireOp",EDGE,"E25.1"),sQuery(id+"F0.wireOp",EDGE,"E25.2"),sQuery(id+"F0.wireOp",EDGE,"E25.3"),sQuery(id+"F0.wireOp",EDGE,"E25.4"),sQuery(id+"F0.wireOp",EDGE,"E25.5"),sQuery(id+"F0.wireOp",EDGE,"E27.0"),sQuery(id+"F0.wireOp",EDGE,"E27.1"),sQuery(id+"F0.wireOp",EDGE,"E27.2"),sQuery(id+"F0.wireOp",EDGE,"E27.3"),sQuery(id+"F0.wireOp",EDGE,"E27.4"),sQuery(id+"F0.wireOp",EDGE,"E27.5")])],"isStart":true}),makeQuery(id+"F6.opExtrude","SWEPT_FACE",FACE,{"disambiguationData":[OSD([sQuery(id+"F5.wireOp",EDGE,"E33.2.1")])]})]});
            var Q15;
            Q15=makeQuery(id+"F6.boolean.opBoolean","INTERSECT",EDGE,{"derivedFrom":[makeQuery(id+"F1.opExtrude","CAP_FACE",FACE,{"disambiguationData":[OSD([sQuery(id+"F0.wireOp",EDGE,"E0"),sQuery(id+"F0.wireOp",EDGE,"E7"),sQuery(id+"F0.wireOp",EDGE,"E8"),sQuery(id+"F0.wireOp",EDGE,"E9"),sQuery(id+"F0.wireOp",EDGE,"E10"),sQuery(id+"F0.wireOp",EDGE,"E11.filletArc"),sQuery(id+"F0.wireOp",EDGE,"E12.filletArc"),sQuery(id+"F0.wireOp",EDGE,"E13.MirrorCS"),sQuery(id+"F0.wireOp",EDGE,"E14.MirrorCS"),sQuery(id+"F0.wireOp",EDGE,"E15"),sQuery(id+"F0.wireOp",EDGE,"E16"),sQuery(id+"F0.wireOp",EDGE,"E17"),sQuery(id+"F0.wireOp",EDGE,"E18"),sQuery(id+"F0.wireOp",EDGE,"E19"),sQuery(id+"F0.wireOp",EDGE,"E20"),sQuery(id+"F0.wireOp",EDGE,"E21"),sQuery(id+"F0.wireOp",EDGE,"E22"),sQuery(id+"F0.wireOp",EDGE,"E23.0"),sQuery(id+"F0.wireOp",EDGE,"E23.1"),sQuery(id+"F0.wireOp",EDGE,"E23.2"),sQuery(id+"F0.wireOp",EDGE,"E23.3"),sQuery(id+"F0.wireOp",EDGE,"E23.4"),sQuery(id+"F0.wireOp",EDGE,"E23.5"),sQuery(id+"F0.wireOp",EDGE,"E24.0"),sQuery(id+"F0.wireOp",EDGE,"E24.1"),sQuery(id+"F0.wireOp",EDGE,"E24.2"),sQuery(id+"F0.wireOp",EDGE,"E24.3"),sQuery(id+"F0.wireOp",EDGE,"E24.4"),sQuery(id+"F0.wireOp",EDGE,"E24.5"),sQuery(id+"F0.wireOp",EDGE,"E25.0"),sQuery(id+"F0.wireOp",EDGE,"E25.1"),sQuery(id+"F0.wireOp",EDGE,"E25.2"),sQuery(id+"F0.wireOp",EDGE,"E25.3"),sQuery(id+"F0.wireOp",EDGE,"E25.4"),sQuery(id+"F0.wireOp",EDGE,"E25.5"),sQuery(id+"F0.wireOp",EDGE,"E27.0"),sQuery(id+"F0.wireOp",EDGE,"E27.1"),sQuery(id+"F0.wireOp",EDGE,"E27.2"),sQuery(id+"F0.wireOp",EDGE,"E27.3"),sQuery(id+"F0.wireOp",EDGE,"E27.4"),sQuery(id+"F0.wireOp",EDGE,"E27.5")])],"isStart":true}),makeQuery(id+"F6.opExtrude","SWEPT_FACE",FACE,{"disambiguationData":[OSD([sQuery(id+"F5.wireOp",EDGE,"E33.2.3")])]})]});
            var Q16;
            Q16=makeQuery(id+"F6.boolean.opBoolean","INTERSECT",EDGE,{"derivedFrom":[makeQuery(id+"F1.opExtrude","CAP_FACE",FACE,{"disambiguationData":[OSD([sQuery(id+"F0.wireOp",EDGE,"E0"),sQuery(id+"F0.wireOp",EDGE,"E7"),sQuery(id+"F0.wireOp",EDGE,"E8"),sQuery(id+"F0.wireOp",EDGE,"E9"),sQuery(id+"F0.wireOp",EDGE,"E10"),sQuery(id+"F0.wireOp",EDGE,"E11.filletArc"),sQuery(id+"F0.wireOp",EDGE,"E12.filletArc"),sQuery(id+"F0.wireOp",EDGE,"E13.MirrorCS"),sQuery(id+"F0.wireOp",EDGE,"E14.MirrorCS"),sQuery(id+"F0.wireOp",EDGE,"E15"),sQuery(id+"F0.wireOp",EDGE,"E16"),sQuery(id+"F0.wireOp",EDGE,"E17"),sQuery(id+"F0.wireOp",EDGE,"E18"),sQuery(id+"F0.wireOp",EDGE,"E19"),sQuery(id+"F0.wireOp",EDGE,"E20"),sQuery(id+"F0.wireOp",EDGE,"E21"),sQuery(id+"F0.wireOp",EDGE,"E22"),sQuery(id+"F0.wireOp",EDGE,"E23.0"),sQuery(id+"F0.wireOp",EDGE,"E23.1"),sQuery(id+"F0.wireOp",EDGE,"E23.2"),sQuery(id+"F0.wireOp",EDGE,"E23.3"),sQuery(id+"F0.wireOp",EDGE,"E23.4"),sQuery(id+"F0.wireOp",EDGE,"E23.5"),sQuery(id+"F0.wireOp",EDGE,"E24.0"),sQuery(id+"F0.wireOp",EDGE,"E24.1"),sQuery(id+"F0.wireOp",EDGE,"E24.2"),sQuery(id+"F0.wireOp",EDGE,"E24.3"),sQuery(id+"F0.wireOp",EDGE,"E24.4"),sQuery(id+"F0.wireOp",EDGE,"E24.5"),sQuery(id+"F0.wireOp",EDGE,"E25.0"),sQuery(id+"F0.wireOp",EDGE,"E25.1"),sQuery(id+"F0.wireOp",EDGE,"E25.2"),sQuery(id+"F0.wireOp",EDGE,"E25.3"),sQuery(id+"F0.wireOp",EDGE,"E25.4"),sQuery(id+"F0.wireOp",EDGE,"E25.5"),sQuery(id+"F0.wireOp",EDGE,"E27.0"),sQuery(id+"F0.wireOp",EDGE,"E27.1"),sQuery(id+"F0.wireOp",EDGE,"E27.2"),sQuery(id+"F0.wireOp",EDGE,"E27.3"),sQuery(id+"F0.wireOp",EDGE,"E27.4"),sQuery(id+"F0.wireOp",EDGE,"E27.5")])],"isStart":true}),makeQuery(id+"F6.opExtrude","SWEPT_FACE",FACE,{"disambiguationData":[OSD([sQuery(id+"F5.wireOp",EDGE,"E34.11.3.0")])]})]});
            var Q17;
            Q17=makeQuery(id+"F6.boolean.opBoolean","INTERSECT",EDGE,{"derivedFrom":[makeQuery(id+"F1.opExtrude","CAP_FACE",FACE,{"disambiguationData":[OSD([sQuery(id+"F0.wireOp",EDGE,"E0"),sQuery(id+"F0.wireOp",EDGE,"E7"),sQuery(id+"F0.wireOp",EDGE,"E8"),sQuery(id+"F0.wireOp",EDGE,"E9"),sQuery(id+"F0.wireOp",EDGE,"E10"),sQuery(id+"F0.wireOp",EDGE,"E11.filletArc"),sQuery(id+"F0.wireOp",EDGE,"E12.filletArc"),sQuery(id+"F0.wireOp",EDGE,"E13.MirrorCS"),sQuery(id+"F0.wireOp",EDGE,"E14.MirrorCS"),sQuery(id+"F0.wireOp",EDGE,"E15"),sQuery(id+"F0.wireOp",EDGE,"E16"),sQuery(id+"F0.wireOp",EDGE,"E17"),sQuery(id+"F0.wireOp",EDGE,"E18"),sQuery(id+"F0.wireOp",EDGE,"E19"),sQuery(id+"F0.wireOp",EDGE,"E20"),sQuery(id+"F0.wireOp",EDGE,"E21"),sQuery(id+"F0.wireOp",EDGE,"E22"),sQuery(id+"F0.wireOp",EDGE,"E23.0"),sQuery(id+"F0.wireOp",EDGE,"E23.1"),sQuery(id+"F0.wireOp",EDGE,"E23.2"),sQuery(id+"F0.wireOp",EDGE,"E23.3"),sQuery(id+"F0.wireOp",EDGE,"E23.4"),sQuery(id+"F0.wireOp",EDGE,"E23.5"),sQuery(id+"F0.wireOp",EDGE,"E24.0"),sQuery(id+"F0.wireOp",EDGE,"E24.1"),sQuery(id+"F0.wireOp",EDGE,"E24.2"),sQuery(id+"F0.wireOp",EDGE,"E24.3"),sQuery(id+"F0.wireOp",EDGE,"E24.4"),sQuery(id+"F0.wireOp",EDGE,"E24.5"),sQuery(id+"F0.wireOp",EDGE,"E25.0"),sQuery(id+"F0.wireOp",EDGE,"E25.1"),sQuery(id+"F0.wireOp",EDGE,"E25.2"),sQuery(id+"F0.wireOp",EDGE,"E25.3"),sQuery(id+"F0.wireOp",EDGE,"E25.4"),sQuery(id+"F0.wireOp",EDGE,"E25.5"),sQuery(id+"F0.wireOp",EDGE,"E27.0"),sQuery(id+"F0.wireOp",EDGE,"E27.1"),sQuery(id+"F0.wireOp",EDGE,"E27.2"),sQuery(id+"F0.wireOp",EDGE,"E27.3"),sQuery(id+"F0.wireOp",EDGE,"E27.4"),sQuery(id+"F0.wireOp",EDGE,"E27.5")])],"isStart":true}),makeQuery(id+"F6.opExtrude","SWEPT_FACE",FACE,{"disambiguationData":[OSD([sQuery(id+"F5.wireOp",EDGE,"E34.6.3.0")])]})]});
            var Q18;
            Q18=makeQuery(id+"F6.boolean.opBoolean","INTERSECT",EDGE,{"derivedFrom":[makeQuery(id+"F1.opExtrude","CAP_FACE",FACE,{"disambiguationData":[OSD([sQuery(id+"F0.wireOp",EDGE,"E0"),sQuery(id+"F0.wireOp",EDGE,"E7"),sQuery(id+"F0.wireOp",EDGE,"E8"),sQuery(id+"F0.wireOp",EDGE,"E9"),sQuery(id+"F0.wireOp",EDGE,"E10"),sQuery(id+"F0.wireOp",EDGE,"E11.filletArc"),sQuery(id+"F0.wireOp",EDGE,"E12.filletArc"),sQuery(id+"F0.wireOp",EDGE,"E13.MirrorCS"),sQuery(id+"F0.wireOp",EDGE,"E14.MirrorCS"),sQuery(id+"F0.wireOp",EDGE,"E15"),sQuery(id+"F0.wireOp",EDGE,"E16"),sQuery(id+"F0.wireOp",EDGE,"E17"),sQuery(id+"F0.wireOp",EDGE,"E18"),sQuery(id+"F0.wireOp",EDGE,"E19"),sQuery(id+"F0.wireOp",EDGE,"E20"),sQuery(id+"F0.wireOp",EDGE,"E21"),sQuery(id+"F0.wireOp",EDGE,"E22"),sQuery(id+"F0.wireOp",EDGE,"E23.0"),sQuery(id+"F0.wireOp",EDGE,"E23.1"),sQuery(id+"F0.wireOp",EDGE,"E23.2"),sQuery(id+"F0.wireOp",EDGE,"E23.3"),sQuery(id+"F0.wireOp",EDGE,"E23.4"),sQuery(id+"F0.wireOp",EDGE,"E23.5"),sQuery(id+"F0.wireOp",EDGE,"E24.0"),sQuery(id+"F0.wireOp",EDGE,"E24.1"),sQuery(id+"F0.wireOp",EDGE,"E24.2"),sQuery(id+"F0.wireOp",EDGE,"E24.3"),sQuery(id+"F0.wireOp",EDGE,"E24.4"),sQuery(id+"F0.wireOp",EDGE,"E24.5"),sQuery(id+"F0.wireOp",EDGE,"E25.0"),sQuery(id+"F0.wireOp",EDGE,"E25.1"),sQuery(id+"F0.wireOp",EDGE,"E25.2"),sQuery(id+"F0.wireOp",EDGE,"E25.3"),sQuery(id+"F0.wireOp",EDGE,"E25.4"),sQuery(id+"F0.wireOp",EDGE,"E25.5"),sQuery(id+"F0.wireOp",EDGE,"E27.0"),sQuery(id+"F0.wireOp",EDGE,"E27.1"),sQuery(id+"F0.wireOp",EDGE,"E27.2"),sQuery(id+"F0.wireOp",EDGE,"E27.3"),sQuery(id+"F0.wireOp",EDGE,"E27.4"),sQuery(id+"F0.wireOp",EDGE,"E27.5")])],"isStart":true}),makeQuery(id+"F6.opExtrude","SWEPT_FACE",FACE,{"disambiguationData":[OSD([sQuery(id+"F5.wireOp",EDGE,"E34.7.3.0")])]})]});
            var Q19;
            Q19=makeQuery(id+"F6.boolean.opBoolean","INTERSECT",EDGE,{"derivedFrom":[makeQuery(id+"F1.opExtrude","CAP_FACE",FACE,{"disambiguationData":[OSD([sQuery(id+"F0.wireOp",EDGE,"E0"),sQuery(id+"F0.wireOp",EDGE,"E7"),sQuery(id+"F0.wireOp",EDGE,"E8"),sQuery(id+"F0.wireOp",EDGE,"E9"),sQuery(id+"F0.wireOp",EDGE,"E10"),sQuery(id+"F0.wireOp",EDGE,"E11.filletArc"),sQuery(id+"F0.wireOp",EDGE,"E12.filletArc"),sQuery(id+"F0.wireOp",EDGE,"E13.MirrorCS"),sQuery(id+"F0.wireOp",EDGE,"E14.MirrorCS"),sQuery(id+"F0.wireOp",EDGE,"E15"),sQuery(id+"F0.wireOp",EDGE,"E16"),sQuery(id+"F0.wireOp",EDGE,"E17"),sQuery(id+"F0.wireOp",EDGE,"E18"),sQuery(id+"F0.wireOp",EDGE,"E19"),sQuery(id+"F0.wireOp",EDGE,"E20"),sQuery(id+"F0.wireOp",EDGE,"E21"),sQuery(id+"F0.wireOp",EDGE,"E22"),sQuery(id+"F0.wireOp",EDGE,"E23.0"),sQuery(id+"F0.wireOp",EDGE,"E23.1"),sQuery(id+"F0.wireOp",EDGE,"E23.2"),sQuery(id+"F0.wireOp",EDGE,"E23.3"),sQuery(id+"F0.wireOp",EDGE,"E23.4"),sQuery(id+"F0.wireOp",EDGE,"E23.5"),sQuery(id+"F0.wireOp",EDGE,"E24.0"),sQuery(id+"F0.wireOp",EDGE,"E24.1"),sQuery(id+"F0.wireOp",EDGE,"E24.2"),sQuery(id+"F0.wireOp",EDGE,"E24.3"),sQuery(id+"F0.wireOp",EDGE,"E24.4"),sQuery(id+"F0.wireOp",EDGE,"E24.5"),sQuery(id+"F0.wireOp",EDGE,"E25.0"),sQuery(id+"F0.wireOp",EDGE,"E25.1"),sQuery(id+"F0.wireOp",EDGE,"E25.2"),sQuery(id+"F0.wireOp",EDGE,"E25.3"),sQuery(id+"F0.wireOp",EDGE,"E25.4"),sQuery(id+"F0.wireOp",EDGE,"E25.5"),sQuery(id+"F0.wireOp",EDGE,"E27.0"),sQuery(id+"F0.wireOp",EDGE,"E27.1"),sQuery(id+"F0.wireOp",EDGE,"E27.2"),sQuery(id+"F0.wireOp",EDGE,"E27.3"),sQuery(id+"F0.wireOp",EDGE,"E27.4"),sQuery(id+"F0.wireOp",EDGE,"E27.5")])],"isStart":true}),makeQuery(id+"F6.opExtrude","SWEPT_FACE",FACE,{"disambiguationData":[OSD([sQuery(id+"F5.wireOp",EDGE,"E34.4.3.0")])]})]});
            var Q20;
            Q20=makeQuery(id+"F6.boolean.opBoolean","INTERSECT",EDGE,{"derivedFrom":[makeQuery(id+"F1.opExtrude","CAP_FACE",FACE,{"disambiguationData":[OSD([sQuery(id+"F0.wireOp",EDGE,"E0"),sQuery(id+"F0.wireOp",EDGE,"E7"),sQuery(id+"F0.wireOp",EDGE,"E8"),sQuery(id+"F0.wireOp",EDGE,"E9"),sQuery(id+"F0.wireOp",EDGE,"E10"),sQuery(id+"F0.wireOp",EDGE,"E11.filletArc"),sQuery(id+"F0.wireOp",EDGE,"E12.filletArc"),sQuery(id+"F0.wireOp",EDGE,"E13.MirrorCS"),sQuery(id+"F0.wireOp",EDGE,"E14.MirrorCS"),sQuery(id+"F0.wireOp",EDGE,"E15"),sQuery(id+"F0.wireOp",EDGE,"E16"),sQuery(id+"F0.wireOp",EDGE,"E17"),sQuery(id+"F0.wireOp",EDGE,"E18"),sQuery(id+"F0.wireOp",EDGE,"E19"),sQuery(id+"F0.wireOp",EDGE,"E20"),sQuery(id+"F0.wireOp",EDGE,"E21"),sQuery(id+"F0.wireOp",EDGE,"E22"),sQuery(id+"F0.wireOp",EDGE,"E23.0"),sQuery(id+"F0.wireOp",EDGE,"E23.1"),sQuery(id+"F0.wireOp",EDGE,"E23.2"),sQuery(id+"F0.wireOp",EDGE,"E23.3"),sQuery(id+"F0.wireOp",EDGE,"E23.4"),sQuery(id+"F0.wireOp",EDGE,"E23.5"),sQuery(id+"F0.wireOp",EDGE,"E24.0"),sQuery(id+"F0.wireOp",EDGE,"E24.1"),sQuery(id+"F0.wireOp",EDGE,"E24.2"),sQuery(id+"F0.wireOp",EDGE,"E24.3"),sQuery(id+"F0.wireOp",EDGE,"E24.4"),sQuery(id+"F0.wireOp",EDGE,"E24.5"),sQuery(id+"F0.wireOp",EDGE,"E25.0"),sQuery(id+"F0.wireOp",EDGE,"E25.1"),sQuery(id+"F0.wireOp",EDGE,"E25.2"),sQuery(id+"F0.wireOp",EDGE,"E25.3"),sQuery(id+"F0.wireOp",EDGE,"E25.4"),sQuery(id+"F0.wireOp",EDGE,"E25.5"),sQuery(id+"F0.wireOp",EDGE,"E27.0"),sQuery(id+"F0.wireOp",EDGE,"E27.1"),sQuery(id+"F0.wireOp",EDGE,"E27.2"),sQuery(id+"F0.wireOp",EDGE,"E27.3"),sQuery(id+"F0.wireOp",EDGE,"E27.4"),sQuery(id+"F0.wireOp",EDGE,"E27.5")])],"isStart":true}),makeQuery(id+"F6.opExtrude","SWEPT_FACE",FACE,{"disambiguationData":[OSD([sQuery(id+"F5.wireOp",EDGE,"E33.1.3")])]})]});
            var Q21;
            Q21=makeQuery(id+"F6.boolean.opBoolean","COPY",EDGE,{"derivedFrom":makeQuery(id+"F6.opExtrude","CAP_EDGE",EDGE,{"disambiguationData":[OSD([sQuery(id+"F5.wireOp",EDGE,"E33.1.0")])],"isStart":true})});
            var Q22;
            Q22=makeQuery(id+"F6.boolean.opBoolean","COPY",EDGE,{"derivedFrom":makeQuery(id+"F6.opExtrude","CAP_EDGE",EDGE,{"disambiguationData":[OSD([sQuery(id+"F5.wireOp",EDGE,"E33.1.2")])],"isStart":true})});
            var Q23;
            Q23=makeQuery(id+"F6.boolean.opBoolean","COPY",EDGE,{"derivedFrom":makeQuery(id+"F6.opExtrude","CAP_EDGE",EDGE,{"disambiguationData":[OSD([sQuery(id+"F5.wireOp",EDGE,"E33.2.3")])],"isStart":true})});
            var Q24;
            Q24=makeQuery(id+"F6.boolean.opBoolean","COPY",EDGE,{"derivedFrom":makeQuery(id+"F6.opExtrude","CAP_EDGE",EDGE,{"disambiguationData":[OSD([sQuery(id+"F5.wireOp",EDGE,"E33.2.2")])],"isStart":true})});
            var Q25;
            Q25=makeQuery(id+"F6.boolean.opBoolean","COPY",EDGE,{"derivedFrom":makeQuery(id+"F6.opExtrude","CAP_EDGE",EDGE,{"disambiguationData":[OSD([sQuery(id+"F5.wireOp",EDGE,"E33.2.1")])],"isStart":true})});
            var Q26;
            Q26=makeQuery(id+"F6.boolean.opBoolean","COPY",EDGE,{"derivedFrom":makeQuery(id+"F6.opExtrude","CAP_EDGE",EDGE,{"disambiguationData":[OSD([sQuery(id+"F5.wireOp",EDGE,"E34.11.3.0")])],"isStart":true})});
            var Q27;
            Q27=makeQuery(id+"F6.boolean.opBoolean","COPY",EDGE,{"derivedFrom":makeQuery(id+"F6.opExtrude","CAP_EDGE",EDGE,{"disambiguationData":[OSD([sQuery(id+"F5.wireOp",EDGE,"E34.7.3.0")])],"isStart":true})});
            var Q28;
            Q28=makeQuery(id+"F6.boolean.opBoolean","COPY",EDGE,{"derivedFrom":makeQuery(id+"F6.opExtrude","CAP_EDGE",EDGE,{"disambiguationData":[OSD([sQuery(id+"F5.wireOp",EDGE,"E34.4.3.0")])],"isStart":true})});
            var Q29;
            Q29=makeQuery(id+"F6.boolean.opBoolean","COPY",EDGE,{"derivedFrom":makeQuery(id+"F6.opExtrude","SWEPT_EDGE",EDGE,{"disambiguationData":[OSD([sQuery(id+"F5.wireOp",EDGE,"E33.1.2"),sQuery(id+"F5.wireOp",EDGE,"E33.1.3")])]})});
            var Q30;
            Q30=makeQuery(id+"F6.boolean.opBoolean","COPY",EDGE,{"derivedFrom":makeQuery(id+"F6.opExtrude","SWEPT_EDGE",EDGE,{"disambiguationData":[OSD([sQuery(id+"F5.wireOp",EDGE,"E33.1.0"),sQuery(id+"F5.wireOp",EDGE,"E33.1.3")])]})});
            var Q31;
            Q31=makeQuery(id+"F6.boolean.opBoolean","COPY",EDGE,{"derivedFrom":makeQuery(id+"F6.opExtrude","CAP_EDGE",EDGE,{"disambiguationData":[OSD([sQuery(id+"F5.wireOp",EDGE,"E33.1.1")])],"isStart":true})});
            var Q32;
            Q32=makeQuery(id+"F6.boolean.opBoolean","COPY",EDGE,{"derivedFrom":makeQuery(id+"F6.opExtrude","SWEPT_EDGE",EDGE,{"disambiguationData":[OSD([sQuery(id+"F5.wireOp",EDGE,"E33.1.1"),sQuery(id+"F5.wireOp",EDGE,"E33.1.2")])]})});
            var Q33;
            Q33=makeQuery(id+"F6.boolean.opBoolean","COPY",EDGE,{"derivedFrom":makeQuery(id+"F6.opExtrude","SWEPT_EDGE",EDGE,{"disambiguationData":[OSD([sQuery(id+"F5.wireOp",EDGE,"E33.1.0"),sQuery(id+"F5.wireOp",EDGE,"E33.1.1")])]})});
            var Q34;
            Q34=makeQuery(id+"F6.boolean.opBoolean","COPY",EDGE,{"derivedFrom":makeQuery(id+"F6.opExtrude","SWEPT_EDGE",EDGE,{"disambiguationData":[OSD([sQuery(id+"F5.wireOp",EDGE,"E33.2.0"),sQuery(id+"F5.wireOp",EDGE,"E33.2.3")])]})});
            var Q35;
            Q35=makeQuery(id+"F6.boolean.opBoolean","COPY",EDGE,{"derivedFrom":makeQuery(id+"F6.opExtrude","SWEPT_EDGE",EDGE,{"disambiguationData":[OSD([sQuery(id+"F5.wireOp",EDGE,"E33.2.2"),sQuery(id+"F5.wireOp",EDGE,"E33.2.3")])]})});
            var Q36;
            Q36=makeQuery(id+"F6.boolean.opBoolean","COPY",EDGE,{"derivedFrom":makeQuery(id+"F6.opExtrude","SWEPT_EDGE",EDGE,{"disambiguationData":[OSD([sQuery(id+"F5.wireOp",EDGE,"E33.2.1"),sQuery(id+"F5.wireOp",EDGE,"E33.2.2")])]})});
            var Q37;
            Q37=makeQuery(id+"F6.boolean.opBoolean","COPY",EDGE,{"derivedFrom":makeQuery(id+"F6.opExtrude","SWEPT_EDGE",EDGE,{"disambiguationData":[OSD([sQuery(id+"F5.wireOp",EDGE,"E33.2.0"),sQuery(id+"F5.wireOp",EDGE,"E33.2.1")])]})});
            var Q38;
            Q38=makeQuery(id+"F6.boolean.opBoolean","COPY",EDGE,{"derivedFrom":makeQuery(id+"F6.opExtrude","SWEPT_EDGE",EDGE,{"disambiguationData":[OSD([sQuery(id+"F5.wireOp",EDGE,"E34.6.3.0"),sQuery(id+"F5.wireOp",EDGE,"E34.11.3.0")])]})});
            var Q39;
            Q39=makeQuery(id+"F6.boolean.opBoolean","COPY",EDGE,{"derivedFrom":makeQuery(id+"F6.opExtrude","SWEPT_EDGE",EDGE,{"disambiguationData":[OSD([sQuery(id+"F5.wireOp",EDGE,"E34.7.3.0"),sQuery(id+"F5.wireOp",EDGE,"E34.11.3.0")])]})});
            var Q40;
            Q40=makeQuery(id+"F6.boolean.opBoolean","COPY",EDGE,{"derivedFrom":makeQuery(id+"F6.opExtrude","SWEPT_EDGE",EDGE,{"disambiguationData":[OSD([sQuery(id+"F5.wireOp",EDGE,"E34.4.3.0"),sQuery(id+"F5.wireOp",EDGE,"E34.7.3.0")])]})});
            var Q41;
            Q41=makeQuery(id+"F6.boolean.opBoolean","COPY",EDGE,{"derivedFrom":makeQuery(id+"F6.opExtrude","SWEPT_EDGE",EDGE,{"disambiguationData":[OSD([sQuery(id+"F5.wireOp",EDGE,"E34.4.3.0"),sQuery(id+"F5.wireOp",EDGE,"E34.6.3.0")])]})});
            fillet(context, id + "F7", {"entities" : qUnion([Q0, Q1, Q2, Q3, Q4, Q5, Q6, Q7, Q8, Q9, Q10, Q11, Q12, Q13, Q14, Q15, Q16, Q17, Q18, Q19, Q20, Q21, Q22, Q23, Q24, Q25, Q26, Q27, Q28, Q29, Q30, Q31, Q32, Q33, Q34, Q35, Q36, Q37, Q38, Q39, Q40, Q41]), "radius" : 0.5 * mm, "tangentPropagation" : true, "allowEdgeOverflow" : false});
        }
    });
